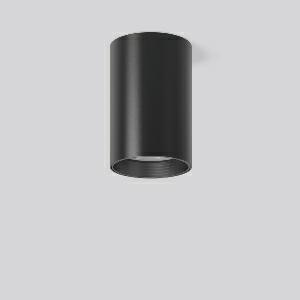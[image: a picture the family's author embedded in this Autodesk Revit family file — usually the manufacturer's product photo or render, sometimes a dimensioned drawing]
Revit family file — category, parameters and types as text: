
# Revit family: heledon_maxi_a_931249_003_2_c4f5
name_source: partatom
category: Lighting Fixtures
units: mm (PartAtom-declared; Revit-internal decimal feet)

## family parameters
Cut with Voids When Loaded = No
Host = Face
Light Source = No
Part Type = Normal
Room Calculation Point = No
Round Connector Dimension = Use Diameter
Shared = No

## types (1)
- HELEDON maxi A (1 x LED Modul 927 bakery, 2850 lm, 2700)
    Apparent Load = 33 VA
    Approval mark = CE
    CIE Flux Codes = 96 99 100 100 100
    Color Rendering = 90
    Color Temperature = 2700
    Default Elevation = 1800 mm
    Description = Series: HELEDON maxi
Cylindrical surface-mounted downlight. Housing: die-cast aluminium, powder-coated. Internal ceiling frame polycarbonate with bayonet mounting. Black plastic ring and recessed LED to prevent glare from the side. Optical assembly with lens made of plastic (polycarbonate) for the best homogeneous light distribution - can be changed without tools. Special LED for illumination of pastries included. Suitable for Ceiling mounting. Easy installation with a separate ceiling frame with bayonet mounting and plug connection. Driver integrated. Connected via plug-in connector. High quality converter without flickering and stroboscopic effect. The following accessories can be mounted without use of tools: interchangeable lenses, decorative glasses, honeycomb louvre, clear and frosted diffusers, white interchangeable plastic ring. 
Colour: deep black, matt (RAL 9005)
Diameter: 123 mm
Height: 183 mm
Lamp: LED
Socket: without socket
Colour temperature: bakery
Colour rendering index (CRI): 97
System power: 33 W
Rated luminous flux: 2850 lm
Luminous efficiency: 86 lm/W
Control gear: Regulated power supply
Protection class: I
Type of protection: IP 20
    Height = 183 mm
    Lamp = 1 x LED Modul 927 bakery
    Lamp Light Flux = 2850 lm
    Lamp count = 1
    Length = 123 mm
    Lifetime = 50000 h
    Luminous efficacy = 86 lm/W
    Manufacturer = RZB
    ModVariant = No
    Model = 931249.003.2
    Mounting Place = Ceiling
    Mounting Type = Surface mounted
    Number of Poles = 1
    OnlyDefault = Yes
    Power Factor = 1
    Product Name = HELEDON maxi A
    Product group = Surface mounted downlights
    ProductGroupID = 302
    Protection Class = Protection class I
    Protection Degree = IP 20
    RLX_Detail_Level = 1
    RLX_Emergency_Light_Flux = 0 lm
    RLX_Emergency_Type = 0
    RLX_Emergency_Type_DB = No
    RlxData = <blob elided: 97001 chars, md5=017da83e>
    Socket = socket
    Standby Power = 0 W
    System Light Flux = 2850 lm
    System Power = 33 W
    Type Comments = Product without accessories
    Type Image = 931193.003.jpg
    URL = http://relux.com
    VarID = ---
    Voltage = 230 V
    Voltage Range = 220-240 V
    Weight = 0.00 kg
    Width = 0 mm  [stored 0 ft]

note: [stored X ft] marks values corroborated as IEEE doubles in the binary element streams (Revit-internal decimal feet)

## geometry (parser evidence)
native form markers: Blend x4, Sweep x10
no freeform markers — native parametric forms only
